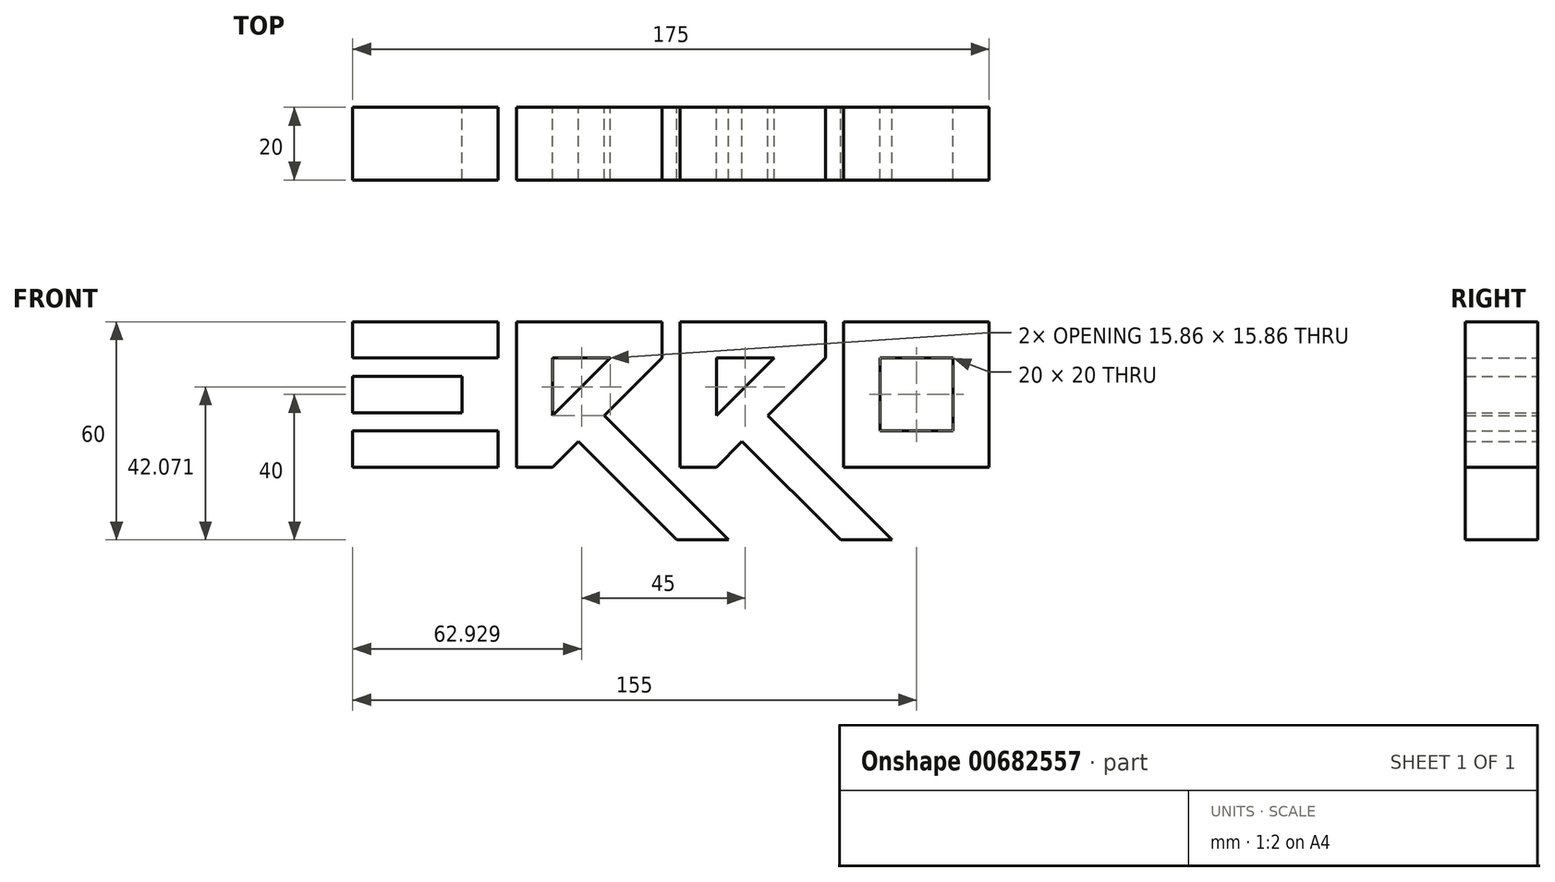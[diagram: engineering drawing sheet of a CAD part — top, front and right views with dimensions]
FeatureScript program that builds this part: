
annotation { "Feature Type Name" : "Feature", "Feature Type Description" : "" }
export const myFeature = defineFeature(function(context is Context, id is Id, definition is map)
    precondition{}
    {
        {
            var Q0;
            Q0=qCreatedBy(makeId("Front.planeOp"),FACE);
            var sketch = newSketch(context, id + "F0", { "sketchPlane" : qUnion([Q0])});
            skLineSegment(sketch, "E0.bottom", {"start": v(0, 0) * mm, "end": v(-40, 0) * mm});
            skLineSegment(sketch, "E0.top", {"start": v(0, 10) * mm, "end": v(-40, 10) * mm});
            skLineSegment(sketch, "E0.left", {"start": v(0, 0) * mm, "end": v(0, 10) * mm});
            skLineSegment(sketch, "E0.right", {"start": v(-40, 0) * mm, "end": v(-40, 10) * mm});
            skLineSegment(sketch, "E1.bottom", {"start": v(-40, 25) * mm, "end": v(-10, 25) * mm});
            skLineSegment(sketch, "E1.top", {"start": v(-40, 15) * mm, "end": v(-10, 15) * mm});
            skLineSegment(sketch, "E1.left", {"start": v(-40, 25) * mm, "end": v(-40, 15) * mm});
            skLineSegment(sketch, "E1.right", {"start": v(-10, 25) * mm, "end": v(-10, 15) * mm});
            skLineSegment(sketch, "E2.bottom", {"start": v(-40, 30) * mm, "end": v(0, 30) * mm});
            skLineSegment(sketch, "E2.top", {"start": v(-40, 40) * mm, "end": v(0, 40) * mm});
            skLineSegment(sketch, "E2.left", {"start": v(-40, 30) * mm, "end": v(-40, 40) * mm});
            skLineSegment(sketch, "E2.right", {"start": v(0, 30) * mm, "end": v(0, 40) * mm});
            skLineSegment(sketch, "E3", {"start": v(5, 0) * mm, "end": v(5, 40) * mm});
            skLineSegment(sketch, "E4", {"start": v(5, 40) * mm, "end": v(45, 40) * mm});
            skLineSegment(sketch, "E5", {"start": v(45, 40) * mm, "end": v(45, 30) * mm});
            skLineSegment(sketch, "E6", {"start": v(15, 0) * mm, "end": v(5, 0) * mm});
            skLineSegment(sketch, "E7", {"start": v(45, 30) * mm, "end": v(29.14, 14.14) * mm});
            skLineSegment(sketch, "E8", {"start": v(15, 0) * mm, "end": v(15, 0) * mm});
            skLineSegment(sketch, "E9", {"start": v(15, 30) * mm, "end": v(30.86, 30) * mm});
            skLineSegment(sketch, "E10", {"start": v(30.86, 30) * mm, "end": v(15, 14.14) * mm});
            skLineSegment(sketch, "E11", {"start": v(15, 14.14) * mm, "end": v(15, 30) * mm});
            skLineSegment(sketch, "E12", {"start": v(22.07, 7.07) * mm, "end": v(49.14, -20) * mm});
            skLineSegment(sketch, "E13", {"start": v(49.14, -20) * mm, "end": v(63.28, -20) * mm});
            skLineSegment(sketch, "E14", {"start": v(63.28, -20) * mm, "end": v(29.14, 14.14) * mm});
            skLineSegment(sketch, "E15", {"start": v(15, 14.14) * mm, "end": v(22.07, 7.07) * mm, "construction": true});
            skLineSegment(sketch, "E16.trimOffspring", {"start": v(22.07, 7.07) * mm, "end": v(15, 0) * mm});
            skLineSegment(sketch, "E17", {"start": v(50, 0) * mm, "end": v(50, 40) * mm});
            skLineSegment(sketch, "E18", {"start": v(50, 40) * mm, "end": v(90, 40) * mm});
            skLineSegment(sketch, "E19", {"start": v(90, 40) * mm, "end": v(90, 30) * mm});
            skLineSegment(sketch, "E20", {"start": v(60, 0) * mm, "end": v(50, 0) * mm});
            skLineSegment(sketch, "E21", {"start": v(90, 30) * mm, "end": v(74.14, 14.14) * mm});
            skLineSegment(sketch, "E22", {"start": v(60, 30) * mm, "end": v(75.86, 30) * mm});
            skLineSegment(sketch, "E23", {"start": v(75.86, 30) * mm, "end": v(60, 14.14) * mm});
            skLineSegment(sketch, "E24", {"start": v(60, 14.14) * mm, "end": v(60, 30) * mm});
            skLineSegment(sketch, "E25", {"start": v(67.07, 7.07) * mm, "end": v(94.14, -20) * mm});
            skLineSegment(sketch, "E26", {"start": v(94.14, -20) * mm, "end": v(108.28, -20) * mm});
            skLineSegment(sketch, "E27", {"start": v(108.28, -20) * mm, "end": v(74.14, 14.14) * mm});
            skLineSegment(sketch, "E28", {"start": v(60, 14.14) * mm, "end": v(67.07, 7.07) * mm, "construction": true});
            skLineSegment(sketch, "E29.trimOffspring", {"start": v(67.07, 7.07) * mm, "end": v(60, 0) * mm});
            skLineSegment(sketch, "E30.bottom", {"start": v(95, 0) * mm, "end": v(135, 0) * mm});
            skLineSegment(sketch, "E30.top", {"start": v(95, 40) * mm, "end": v(135, 40) * mm});
            skLineSegment(sketch, "E30.left", {"start": v(95, 0) * mm, "end": v(95, 40) * mm});
            skLineSegment(sketch, "E30.right", {"start": v(135, 0) * mm, "end": v(135, 40) * mm});
            skLineSegment(sketch, "E31.bottom", {"start": v(105, 30) * mm, "end": v(125, 30) * mm});
            skLineSegment(sketch, "E31.top", {"start": v(105, 10) * mm, "end": v(125, 10) * mm});
            skLineSegment(sketch, "E31.left", {"start": v(105, 30) * mm, "end": v(105, 10) * mm});
            skLineSegment(sketch, "E31.right", {"start": v(125, 30) * mm, "end": v(125, 10) * mm});
            skSolve(sketch);
        }
        {
            var Q0;
            Q0=makeQuery(id+"F0.imprint","IMPRINT",FACE,{"disambiguationData":[TD([[makeQuery(id+"F0.imprint","IMPRINT",EDGE,{"derivedFrom":sQuery(id+"F0.wireOp",EDGE,"E2.bottom")}),1.0]])]});
            var Q1;
            Q1=makeQuery(id+"F0.imprint","IMPRINT",FACE,{"disambiguationData":[TD([[makeQuery(id+"F0.imprint","IMPRINT",EDGE,{"derivedFrom":sQuery(id+"F0.wireOp",EDGE,"E1.bottom")}),-1.0]])]});
            var Q2;
            Q2=makeQuery(id+"F0.imprint","IMPRINT",FACE,{"disambiguationData":[TD([[makeQuery(id+"F0.imprint","IMPRINT",EDGE,{"derivedFrom":sQuery(id+"F0.wireOp",EDGE,"E0.bottom")}),-1.0]])]});
            var Q3;
            Q3=makeQuery(id+"F0.imprint","IMPRINT",FACE,{"disambiguationData":[TD([[makeQuery(id+"F0.imprint","IMPRINT",EDGE,{"derivedFrom":sQuery(id+"F0.wireOp",EDGE,"E3")}),-1.0]])]});
            var Q4;
            {var subQ3=sQuery(id+"F0.wireOp",EDGE,"E18");Q4=makeQuery(id+"F0.imprint","IMPRINT",FACE,{"disambiguationData":[TD([[makeQuery(id+"F0.imprint","IMPRINT",EDGE,{"derivedFrom":subQ3}),-1.0]])]});}
            var Q5;
            Q5=makeQuery(id+"F0.imprint","IMPRINT",FACE,{"disambiguationData":[TD([[makeQuery(id+"F0.imprint","IMPRINT",EDGE,{"derivedFrom":sQuery(id+"F0.wireOp",EDGE,"E30.bottom")}),1.0]])]});
            extrude(context, id + "F1", {"entities" : qUnion([Q0, Q1, Q2, Q3, Q4, Q5]), "depth" : 20 * mm, "offsetDistance" : 25 * mm});
        }
    });
